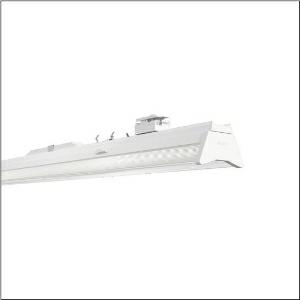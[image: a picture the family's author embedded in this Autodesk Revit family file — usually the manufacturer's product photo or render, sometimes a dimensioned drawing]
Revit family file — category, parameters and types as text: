
# Revit family: licross_r__21_performance_mo_52tm16cn445g_ee6e
name_source: partatom
category: Lighting Fixtures
units: mm (PartAtom-declared; Revit-internal decimal feet)

## family parameters
Cut with Voids When Loaded = No
Host = Face
Light Source = No
Part Type = Normal
Room Calculation Point = No
Round Connector Dimension = Use Diameter
Shared = No

## types (1)
- --- (1 x LED, 4500 lm, 24.1 W, 4000K)
    Apparent Load = 24 VA
    CIE Flux Codes = 66 88 96 79 100
    Color Rendering = 80
    Color Temperature = 4000K
    Default Elevation = 1800 mm
    Description = Licross® 21 Performance MO, luminaire insert, of sheet steel, galvanised, coil coated, white, length: 1.500mm, width: 120mm, height: 123mm, LED rated luminous flux: 4.500lm, light colour: 840, control gear: ON/OFF Multilumen, CLOi, control gear: ECG Multilumen, with plug, 3-pole, with phase selection, mains connection: 220..240V, AC, 50/60Hz, start of lifetime: 24W, end of service life: 28W, internal wiring halogen-free, primary light control with lens, of plastic, primary optical cover: cover, of PMMA, CAT 2 (L<= 3000cd/m²), light emission: direct/indirect distribution, primary light characteristic: symmetric, protection rating (complete): IP40, insulation class (complete): insulation class I (protective earthing), certification: CE, ENEC, UKCA, protection symbol: D if used in an environment without relevant dust loads with corresponding accessories, impact resistance: IK06, permissible ambient temperature for indoor applications: -35..+55°C, corresponds to IFS (International Featured Standards) requirements for safety and quality in the food industry, reducing of maximum allowable ambient temperature of 5°C with ceiling mounting, LABS conformity tested according to VDMA 24364:2018-05, packaging unit: 1 piece
    Height = 114 mm
    Lamp = 1 x LED
    Lamp Light Flux = 4500 lm
    Lamp Power = 24.1 W
    Lamp count = 1
    Length = 1500 mm
    Luminous efficacy = 187 lm/W
    Manufacturer = Siteco
    ModVariant = No
    Model = 52TM16CN445G
    Mounting Place = Ceiling
    Mounting Type = Pendant
    Number of Poles = 1
    OnlyDefault = Yes
    Power Factor = 1
    Product Name = Licross® 21 Performance MO
    Product group = luminaire insert | ceiling pendant
    ProductGroupID = 902
    Protection Class = Protection class I
    Protection Degree = IP 40
    RLX_Detail_Level = 1
    RLX_Emergency_Light_Flux = 0 lm
    RLX_Emergency_Type = 0
    RLX_Emergency_Type_DB = No
    RlxData = <blob elided: 31525 chars, md5=997a15aa>
    Socket = socket
    Standby Power = 0 W
    System Light Flux = 4500 lm
    System Power = 24 W
    Type Comments = factory setting: luminous flux: 100 % | (A | C | E) | 55 mA
    Type Image = l_1256138.jpg
    URL = http://relux.com
    VarID = @adj_069959
    Voltage = 0 V
    Weight = 0.00 kg
    Width = 120 mm

## geometry (parser evidence)
native form markers: Blend x4, Sweep x11
no freeform markers — native parametric forms only
